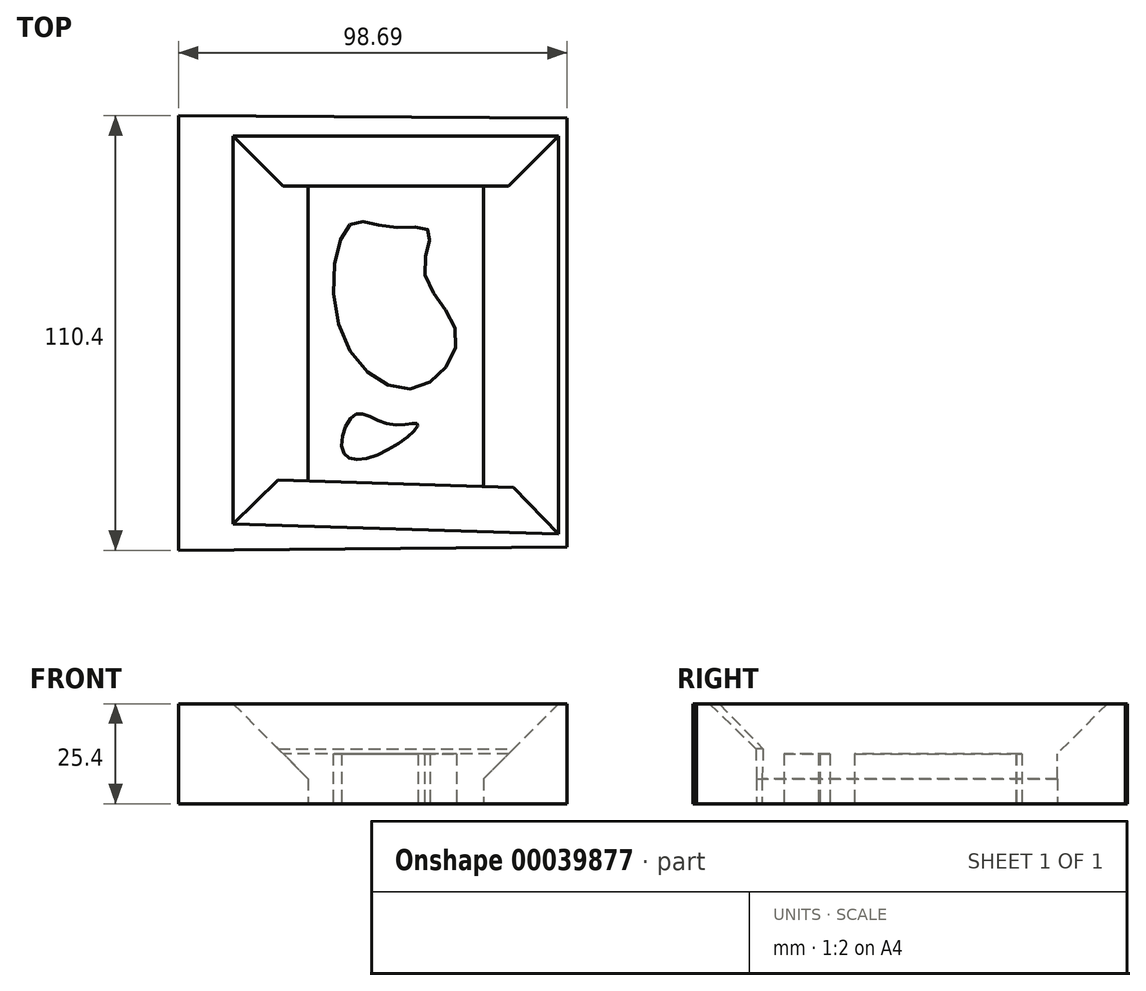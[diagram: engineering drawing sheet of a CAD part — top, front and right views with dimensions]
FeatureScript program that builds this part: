
annotation { "Feature Type Name" : "Feature", "Feature Type Description" : "" }
export const myFeature = defineFeature(function(context is Context, id is Id, definition is map)
    precondition{}
    {
        {
            var Q0;
            Q0=qCreatedBy(makeId("Top.planeOp"),FACE);
            var sketch = newSketch(context, id + "F0", { "sketchPlane" : qUnion([Q0])});
            skLineSegment(sketch, "E0", {"start": v(-53.39, 62.73) * mm, "end": v(-53.39, -47.67) * mm});
            skLineSegment(sketch, "E1", {"start": v(-53.39, 62.73) * mm, "end": v(-20.5, 44.88) * mm});
            skLineSegment(sketch, "E2", {"start": v(-20.5, 44.88) * mm, "end": v(-20.5, -30.1) * mm});
            skLineSegment(sketch, "E3", {"start": v(-20.5, -30.1) * mm, "end": v(-53.39, -47.67) * mm});
            skLineSegment(sketch, "E4", {"start": v(24.11, 44.88) * mm, "end": v(24.11, -31.5) * mm});
            skLineSegment(sketch, "E5", {"start": v(24.11, -31.5) * mm, "end": v(45.3, -46.84) * mm});
            skLineSegment(sketch, "E6", {"start": v(45.3, -46.84) * mm, "end": v(45.3, 62.17) * mm});
            skLineSegment(sketch, "E7", {"start": v(24.11, 44.88) * mm, "end": v(45.3, 62.17) * mm});
            skLineSegment(sketch, "E8", {"start": v(-53.39, -47.67) * mm, "end": v(45.3, -46.84) * mm});
            skLineSegment(sketch, "E9", {"start": v(-20.5, -30.1) * mm, "end": v(24.11, -31.5) * mm});
            skLineSegment(sketch, "E10", {"start": v(-20.5, 44.88) * mm, "end": v(24.11, 44.88) * mm});
            skLineSegment(sketch, "E11", {"start": v(-53.39, 62.73) * mm, "end": v(45.3, 62.17) * mm});
            skSolve(sketch);
        }
        {
            var Q0;
            Q0=makeQuery(id+"F0.imprint","IMPRINT",FACE,{"disambiguationData":[TD([[makeQuery(id+"F0.imprint","IMPRINT",EDGE,{"derivedFrom":sQuery(id+"F0.wireOp",EDGE,"E0")}),1.0]])]});
            var Q1;
            Q1=makeQuery(id+"F0.imprint","IMPRINT",FACE,{"disambiguationData":[TD([[makeQuery(id+"F0.imprint","IMPRINT",EDGE,{"derivedFrom":sQuery(id+"F0.wireOp",EDGE,"E1")}),1.0]])]});
            var Q2;
            Q2=makeQuery(id+"F0.imprint","IMPRINT",FACE,{"disambiguationData":[TD([[makeQuery(id+"F0.imprint","IMPRINT",EDGE,{"derivedFrom":sQuery(id+"F0.wireOp",EDGE,"E4")}),1.0]])]});
            var Q3;
            Q3=makeQuery(id+"F0.imprint","IMPRINT",FACE,{"disambiguationData":[TD([[makeQuery(id+"F0.imprint","IMPRINT",EDGE,{"derivedFrom":sQuery(id+"F0.wireOp",EDGE,"E3")}),1.0]])]});
            extrude(context, id + "F1", {"entities" : qUnion([Q0, Q1, Q2, Q3]), "depth" : 25.4 * mm});
        }
        {
            var Q0;
            Q0=makeQuery(id+"F1.opExtrude","CAP_EDGE",EDGE,{"disambiguationData":[OSD([sQuery(id+"F0.wireOp",EDGE,"E2")])],"isStart":false});
            var Q1;
            Q1=makeQuery(id+"F1.opExtrude","CAP_EDGE",EDGE,{"disambiguationData":[OSD([sQuery(id+"F0.wireOp",EDGE,"E4")])],"isStart":false});
            chamfer(context, id + "F2", {"entities" : qUnion([Q0, Q1]), "width" : 19.05 * mm, "tangentPropagation" : true});
        }
        {
            var Q0;
            Q0=makeQuery(id+"F1.opExtrude","CAP_EDGE",EDGE,{"disambiguationData":[OSD([sQuery(id+"F0.wireOp",EDGE,"E10")])],"isStart":false});
            chamfer(context, id + "F3", {"entities" : qUnion([Q0]), "width" : 12.7 * mm, "tangentPropagation" : true});
        }
        {
            var Q0;
            Q0=makeQuery(id+"F1.opExtrude","CAP_EDGE",EDGE,{"disambiguationData":[OSD([sQuery(id+"F0.wireOp",EDGE,"E9")])],"isStart":false});
            chamfer(context, id + "F4", {"entities" : qUnion([Q0]), "width" : 11.43 * mm, "tangentPropagation" : true});
        }
        {
            var Q0;
            Q0=qCreatedBy(makeId("Top.planeOp"),FACE);
            var sketch = newSketch(context, id + "F5", { "sketchPlane" : qUnion([Q0])});
            skFitSpline(sketch, "E12", {"points": [v(-11.42, -23.13) * mm, v(0, -22.04) * mm, v(7.33, -15.59) * mm, v(0, -15.63) * mm, v(-8.6, -13.2) * mm, v(-11.42, -23.13) * mm]});
            skFitSpline(sketch, "E13", {"points": [v(-9.8, 35.12) * mm, v(-12.04, 7.47) * mm, v(7, -6.42) * mm, v(17.16, 7.33) * mm, v(9.13, 22.73) * mm, v(10.18, 33.5) * mm, v(0, 34.48) * mm, v(-9.8, 35.12) * mm]});
            skSolve(sketch);
        }
        {
            var Q0;
            Q0=makeQuery(id+"F5.imprint","IMPRINT",FACE,{"disambiguationData":[TD([[makeQuery(id+"F5.imprint","IMPRINT",EDGE,{"derivedFrom":sQuery(id+"F5.wireOp",EDGE,"E13")}),1.0]])]});
            var Q1;
            Q1=makeQuery(id+"F5.imprint","IMPRINT",FACE,{"disambiguationData":[TD([[makeQuery(id+"F5.imprint","IMPRINT",EDGE,{"derivedFrom":sQuery(id+"F5.wireOp",EDGE,"E12")}),1.0]])]});
            extrude(context, id + "F6", {"entities" : qUnion([Q0, Q1]), "depth" : 12.7 * mm});
        }
    });
